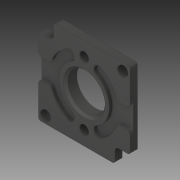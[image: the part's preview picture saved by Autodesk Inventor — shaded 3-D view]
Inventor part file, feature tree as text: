
AUTODESK INVENTOR PART (.ipt)
format: ipt  version: 2019 (Build 230136000, 136)  size: 256,512 bytes
history: native  units: in
note: dims shown in document units (in); Inventor stores cm internally (conversion verified against a paired STEP export)
features: fillet x1
ambient origin geometry x8: Origin, YZ Plane, XZ Plane, XY Plane, X Axis, Y Axis, Z Axis, Center Point
bodies: Solid1 (feature_tree)
feature tree (1):
  fillet  "Fillet4"  [1 undecoded]
note: 1 required parameter value undecoded (feature->parameter linkage not recoverable at this tier; creation-order binding heuristic only, values carry confidence <= 0.55)
